# Revit family: QF_ELECTROLUXPROFESSIONAL_1LSN49_TE1120HP_HP
name_source: partatom
category: Attrezzature speciali
units: mm (PartAtom-declared; Revit-internal decimal feet)

## family parameters
Basato su piano di lavoro = No
Condiviso = No
Punto di calcolo locali = No
Quota connettore circolare = Usa diametro
Sempre verticale = Sì
Taglio con vuoti quando caricato = No
Tipo di parte = Normale

## types (3) — shared parameters
Cycle = 50 Hz
Depth Actual = 625 mm
Height Actual = 850 mm  [stored 2.78871 ft]
Latent Heat Output = 0.0
Length Actual = 596 mm
Modello = TE1120HP
Phase = 1
Produttore = Electrolux Professional
Sensible Heat Output = 0.0
URL = www.electroluxprofessional.com
Volts = 230 V
Watts = 900 W
Weight = 44
zero-valued in all types: Gas KW, Prospetto di default, Steam Pounds per Hour

## per-type parameters (varying)
| type | Descrizione | Item Number |
| 916099832 | myPRO SMART PROFESSIONAL TUMBLE DRYER TE1120HP 8KG HEAT PUMP 230/50/1N 0,9KW DE SCHUKO SST/DARK BLUE | 1LT6EZ |
| 916099831 | myPRO SMART PROFESSIONAL TUMBLE DRYER TE1120HP 8KG HEAT PUMP 230/50/1N 0,9KW SYMBOLS SCHUKO SST/DARK BLUE | 1LT6EY |
| 916099802 | myPRO SMART PROFESSIONAL TUMBLE DRYER TE1120HP 8KG HEAT PUMP 230/50/1N 0,9KW EN PLUG-UK SST | 1LT6EW |

note: [stored X ft] marks values corroborated as IEEE doubles in the binary element streams (Revit-internal decimal feet)

## geometry (parser evidence)
native form markers: Sweep x1
no freeform markers — native parametric forms only
